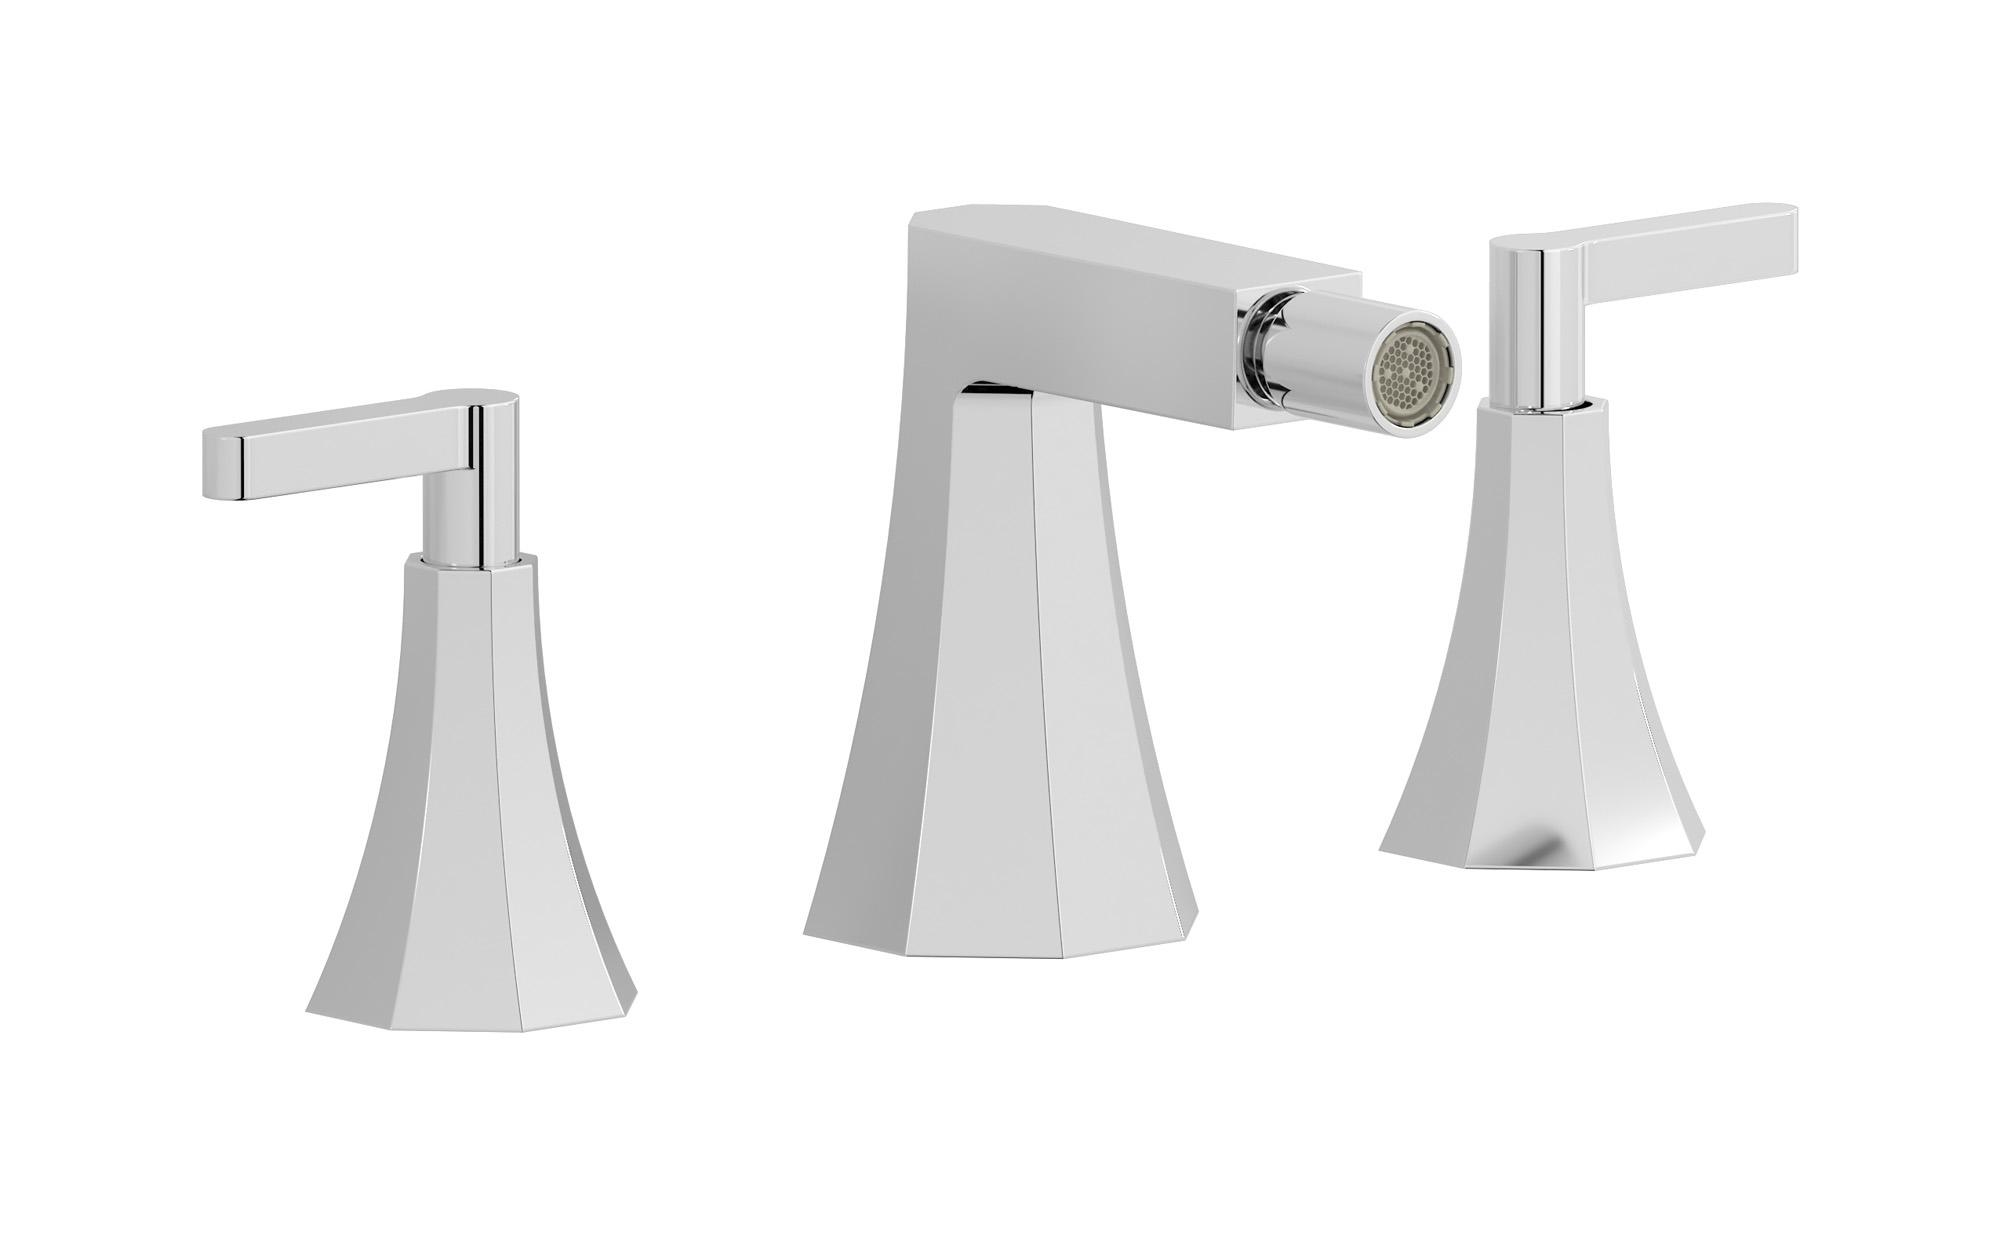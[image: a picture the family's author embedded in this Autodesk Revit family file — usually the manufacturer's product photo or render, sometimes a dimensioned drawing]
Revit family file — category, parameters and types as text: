
# Revit family: BL393
name_source: partatom
category: Apparecchi idraulici
units: mm (PartAtom-declared; Revit-internal decimal feet)

## family parameters
Basato su piano di lavoro = No
Condiviso = No
Mantieni orientamento annotazione = No
Numero OmniClass = 23.45.55.17
Punto di calcolo locali = No
Quota connettore circolare = Usa diametro
Sempre verticale = Sì
Taglio con vuoti quando caricato = No
Tipo di parte = Normale
Titolo OmniClass = Mixing Faucets

## types (7) — shared parameters
Cold water inlet = 10 mm  [stored 0.0328084 ft]
Commenti sul tipo = Bidet set
Connessione CW = No
Connessione HW = No
Connessione di scarico = No
Connessione di ventilazione = No
Descrizione = Three holes bidet set
Hot water inlet = 10 mm  [stored 0.0328084 ft]
Produttore = IB Rubinetterie S.p.A.
URL = https://www.weareib.it
zero-valued in all types: Prospetto di default

## per-type parameters (varying)
| type | Finishes surface | Immagine tipo | Modello |
| Chrome | IB_Chrome | BL393CC.jpg | BL393CC |
| Platinum | IB_Platinum | BL393PL.jpg | BL393PL |
| Rose gold | IB_Rose gold | BL393RS.jpg | BL393RS |
| Gold | IB_gold | BL393OO.jpg | BL393OO |
| Pale gold | IB_Pale gold | BL393II.jpg | BL393II |
| Modern Bronze | IB_Chrome | BL393MB.jpg | BL393MB |
| Brushed Nickel | IB_Brushed nickel | BL393SS.jpg | BL393SS |

note: [stored X ft] marks values corroborated as IEEE doubles in the binary element streams (Revit-internal decimal feet)
